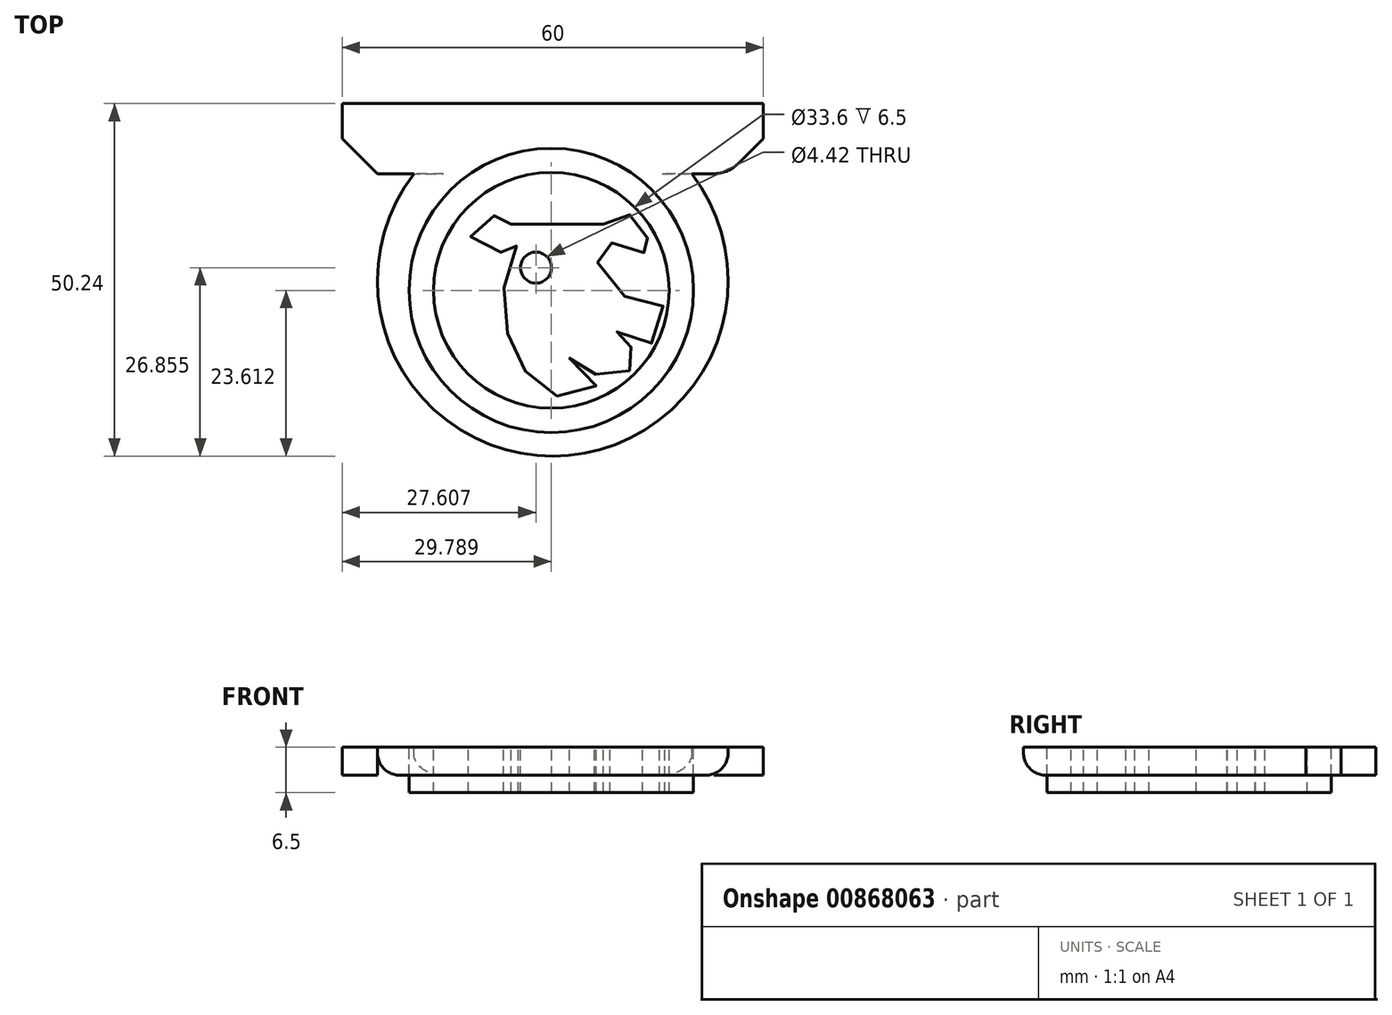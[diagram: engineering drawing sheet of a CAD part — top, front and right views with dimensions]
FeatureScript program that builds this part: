
annotation { "Feature Type Name" : "Feature", "Feature Type Description" : "" }
export const myFeature = defineFeature(function(context is Context, id is Id, definition is map)
    precondition{}
    {
        {
            var Q0;
            Q0=qCreatedBy(makeId("Top.planeOp"),FACE);
            var sketch = newSketch(context, id + "F0", { "sketchPlane" : qUnion([Q0])});
            skCircle(sketch, "E0", {"center": v(0, 1.5) * mm, "radius": 25 * mm});
            skLineSegment(sketch, "E1.bottom", {"start": v(-30, 26.74) * mm, "end": v(30, 26.74) * mm});
            skLineSegment(sketch, "E1.top", {"start": v(-30, 16.74) * mm, "end": v(30, 16.74) * mm});
            skLineSegment(sketch, "E1.left", {"start": v(-30, 26.74) * mm, "end": v(-30, 16.74) * mm});
            skLineSegment(sketch, "E1.right", {"start": v(30, 26.74) * mm, "end": v(30, 16.74) * mm});
            skPoint(sketch, "E1.middle", {"position": v(0, 21.74) * mm});
            skSolve(sketch);
        }
        {
            var Q0;
            Q0=makeQuery(id+"F0.imprint","IMPRINT",FACE,{"disambiguationData":[TD([[makeQuery(id+"F0.imprint","IMPRINT",EDGE,{"derivedFrom":sQuery(id+"F0.wireOp",EDGE,"E0")}),1.0]])]});
            var Q1;
            Q1=makeQuery(id+"F0.imprint","IMPRINT",FACE,{"disambiguationData":[TD([[makeQuery(id+"F0.imprint","IMPRINT",EDGE,{"derivedFrom":sQuery(id+"F0.wireOp",EDGE,"E1.bottom")}),-1.0]])]});
            extrude(context, id + "F1", {"entities" : qUnion([Q0, Q1]), "oppositeDirection" : true, "depth" : 4 * mm, "offsetDistance" : 25 * mm});
        }
        {
            var Q0;
            Q0=makeQuery(id+"F1.opExtrude","CAP_FACE",FACE,{"disambiguationData":[OSD([sQuery(id+"F0.wireOp",EDGE,"E0")])],"isStart":true});
            var sketch = newSketch(context, id + "F2", { "sketchPlane" : qUnion([Q0])});
            skCircle(sketch, "E2", {"center": v(-0.21, 0.11) * mm, "radius": 20.27 * mm});
            skPoint(sketch, "E2.first.point", {"position": v(-20.47, 0.75) * mm});
            skPoint(sketch, "E2.second.point", {"position": v(20.05, 0.75) * mm});
            skPoint(sketch, "E2.third.point", {"position": v(-0.46, 20.38) * mm});
            skCircle(sketch, "E3", {"center": v(-0.21, 0.11) * mm, "radius": 16.8 * mm});
            skCircle(sketch, "E4", {"center": v(-2.4, 3.35) * mm, "radius": 2.21 * mm});
            skPoint(sketch, "E4.first.point", {"position": v(-4.6, 3.44) * mm});
            skPoint(sketch, "E4.second.point", {"position": v(-0.18, 3.4) * mm});
            skPoint(sketch, "E4.third.point", {"position": v(-2.2, 5.56) * mm});
            skLineSegment(sketch, "E5", {"start": v(-5.96, 9.54) * mm, "end": v(7.23, 9.54) * mm});
            skFitSpline(sketch, "E6", {"points": [v(7.23, 9.54) * mm, v(7.52, 9.54) * mm, v(8.13, 9.75) * mm, v(8.6, 10) * mm, v(9.3, 10.53) * mm, v(9.96, 10.81) * mm, v(10.49, 10.9) * mm, v(12.05, 10.88) * mm, v(12.18, 10.8) * mm, v(12.24, 10.54) * mm, v(12.35, 10) * mm, v(12.8, 8.84) * mm, v(13.39, 7.77) * mm, v(14.02, 7.05) * mm, v(14.93, 6.32) * mm, v(15.18, 6.08) * mm, v(15.18, 5.8) * mm, v(15, 5.57) * mm, v(14.59, 5.51) * mm, v(11.17, 5.52) * mm, v(10.84, 5.56) * mm, v(9.87, 6.07) * mm, v(9.26, 6.43) * mm, v(8.83, 6.68) * mm, v(8.46, 6.87) * mm, v(8.15, 6.9) * mm, v(6.14, 6.93) * mm, v(5.99, 6.89) * mm, v(5.94, 6.72) * mm, v(6.03, 5.67) * mm, v(6.36, 4.14) * mm, v(7.07, 2.5) * mm, v(7.98, 1.22) * mm, v(9.03, 0.12) * mm, v(10.34, -0.77) * mm, v(11.98, -1.45) * mm, v(13.56, -1.8) * mm, v(15.11, -1.91) * mm, v(15.54, -2) * mm, v(15.81, -2.25) * mm, v(15.98, -2.58) * mm, v(15.89, -3.16) * mm, v(15.2, -5.45) * mm, v(14.32, -7.16) * mm, v(13.93, -7.48) * mm, v(13.37, -7.6) * mm, v(12.88, -7.57) * mm, v(11.21, -6.97) * mm, v(9.76, -6.18) * mm, v(8.91, -5.67) * mm, v(8.58, -5.62) * mm, v(8.32, -5.74) * mm, v(8.2, -6.01) * mm, v(8.2, -6.3) * mm, v(9.27, -7.05) * mm, v(11.5, -8.1) * mm, v(12.4, -8.43) * mm, v(12.7, -8.7) * mm, v(12.77, -9.26) * mm, v(12.47, -9.87) * mm, v(11.13, -11.17) * mm, v(9.23, -12.6) * mm, v(8.6, -12.92) * mm, v(7.95, -12.97) * mm, v(7.6, -12.91) * mm, v(6.03, -11.78) * mm, v(3.74, -9.66) * mm, v(3.26, -9.1) * mm, v(3.07, -8.95) * mm, v(2.74, -8.94) * mm, v(2.45, -9.2) * mm, v(2.4, -9.52) * mm, v(2.56, -9.8) * mm, v(3.73, -11.02) * mm, v(5.36, -12.51) * mm, v(6.08, -13.09) * mm, v(6.19, -13.4) * mm, v(6.13, -13.76) * mm, v(5.81, -14.15) * mm, v(3.84, -14.68) * mm, v(1.76, -14.9) * mm, v(0.28, -14.9) * mm, v(-0.56, -14.66) * mm, v(-1.5, -14.11) * mm, v(-2.72, -12.9) * mm, v(-3.92, -11.4) * mm, v(-4.9, -9.75) * mm, v(-5.48, -8.54) * mm, v(-5.92, -7.5) * mm, v(-6.35, -6.26) * mm, v(-6.74, -4.64) * mm, v(-6.98, -2.94) * mm, v(-7.03, -0.9) * mm, v(-6.95, 0.57) * mm, v(-6.6, 2.72) * mm, v(-6, 4.61) * mm, v(-5.65, 5.48) * mm, v(-5.2, 6.44) * mm, v(-4.97, 6.84) * mm, v(-4.97, 6.96) * mm, v(-6.14, 6.93) * mm, v(-6.23, 6.9) * mm, v(-6.3, 6.84) * mm, v(-6.58, 6.43) * mm, v(-7.06, 5.74) * mm, v(-7.3, 5.54) * mm, v(-7.97, 5.53) * mm, v(-8.4, 5.63) * mm, v(-9.3, 5.96) * mm, v(-10.3, 6.54) * mm, v(-11.22, 7.28) * mm, v(-12.05, 8.2) * mm, v(-12.03, 8.23) * mm, v(-11.31, 9.03) * mm, v(-10.38, 9.81) * mm, v(-9.23, 10.48) * mm, v(-8.17, 10.82) * mm, v(-7.77, 10.9) * mm, v(-7.1, 10.9) * mm, v(-6.79, 10.69) * mm, v(-6.51, 10.19) * mm, v(-6.4, 9.83) * mm, v(-6.33, 9.64) * mm, v(-6.2, 9.54) * mm, v(-5.96, 9.54) * mm], "startDerivative": vector(55.31, -6.4) * mm, "endDerivative": vector(59.6, 6.66) * mm});
            skSolve(sketch);
        }
        {
            var Q0;
            Q0=makeQuery(id+"F2.imprint","IMPRINT",FACE,{"disambiguationData":[TD([[makeQuery(id+"F2.imprint","IMPRINT",EDGE,{"derivedFrom":sQuery(id+"F2.wireOp",EDGE,"E4")}),-1.0]])]});
            var Q1;
            Q1=makeQuery(id+"F2.imprint","IMPRINT",FACE,{"disambiguationData":[TD([[makeQuery(id+"F2.imprint","IMPRINT",EDGE,{"derivedFrom":sQuery(id+"F2.wireOp",EDGE,"E2")}),1.0]])]});
            var Q2;
            Q2=makeQuery(id+"F1.opExtrude","CAP_FACE",FACE,{"disambiguationData":[OSD([sQuery(id+"F0.wireOp",EDGE,"GiU07cMu-9cvY-aq7m-KHih-6PXQR21th8sj.bottom"),sQuery(id+"F0.wireOp",EDGE,"GiU07cMu-9cvY-aq7m-KHih-6PXQR21th8sj.top"),sQuery(id+"F0.wireOp",EDGE,"GiU07cMu-9cvY-aq7m-KHih-6PXQR21th8sj.left"),sQuery(id+"F0.wireOp",EDGE,"P3Z4kugq-KXoC-PKu6-b1Nk-Jbw3Nn5FDpoZ"),sQuery(id+"F0.wireOp",EDGE,"qLsFG4fF-1ukw-phWH-hEqs-MhgE6pIn2S9s")])],"isStart":true});
            var Q3;
            Q3=makeQuery(id+"F1.opExtrude","SWEPT_BODY",BODY,{"disambiguationData":[OSD([sQuery(id+"F0.wireOp",EDGE,"GiU07cMu-9cvY-aq7m-KHih-6PXQR21th8sj.bottom"),sQuery(id+"F0.wireOp",EDGE,"GiU07cMu-9cvY-aq7m-KHih-6PXQR21th8sj.top"),sQuery(id+"F0.wireOp",EDGE,"GiU07cMu-9cvY-aq7m-KHih-6PXQR21th8sj.left"),sQuery(id+"F0.wireOp",EDGE,"P3Z4kugq-KXoC-PKu6-b1Nk-Jbw3Nn5FDpoZ"),sQuery(id+"F0.wireOp",EDGE,"qLsFG4fF-1ukw-phWH-hEqs-MhgE6pIn2S9s")])]});
            extrude(context, id + "F3", {"entities" : qUnion([Q0, Q1]), "oppositeDirection" : true, "depth" : 6.5 * mm, "endBoundEntityFace" : qUnion([Q2]), "endBoundEntityBody" : qUnion([Q3]), "offsetDistance" : 25 * mm});
        }
        {
            var Q0;
            Q0=makeQuery(id+"F1.opExtrude","SWEPT_EDGE",EDGE,{"disambiguationData":[OSD([sQuery(id+"F0.wireOp",EDGE,"E1.top"),sQuery(id+"F0.wireOp",EDGE,"E1.right")])]});
            var Q1;
            Q1=makeQuery(id+"F1.opExtrude","SWEPT_EDGE",EDGE,{"disambiguationData":[OSD([sQuery(id+"F0.wireOp",EDGE,"E1.top"),sQuery(id+"F0.wireOp",EDGE,"E1.left")])]});
            chamfer(context, id + "F4", {"entities" : qUnion([Q0, Q1]), "width" : 5 * mm, "tangentPropagation" : true});
        }
        {
            var Q0;
            Q0=makeQuery(id+"F1.opExtrude","CAP_EDGE",EDGE,{"disambiguationData":[OSD([sQuery(id+"F0.wireOp",EDGE,"E0")])],"isStart":false});
            fillet(context, id + "F5", {"entities" : qUnion([Q0]), "tangentPropagation" : true, "radius" : 3.2 * mm, "defaultsChanged" : true, "vertexSettings" : [], "allowEdgeOverflow" : false});
        }
        {
            var Q0;
            {var subQ0=sQuery(id+"F0.wireOp",EDGE,"E1.top");var subQ1=sQuery(id+"F0.wireOp",EDGE,"E1.left");Q0=makeQuery(id+"F4.opChamfer","BLEND_EDGE",EDGE,{"blendedFrom":[makeQuery(id+"F1.opExtrude","SWEPT_EDGE",EDGE,{"disambiguationData":[OSD([subQ0,subQ1])]}),makeQuery(id+"F1.opExtrude","SWEPT_FACE",FACE,{"disambiguationData":[OSD([subQ0]),TDD([makeQuery(id+"F0.imprint","IMPRINT",EDGE,{"disambiguationData":[TD([[makeQuery(id+"F0.imprint","INTERSECT",VERTEX,{"disambiguationData":[OD(0.0)],"derivedFrom":[sQuery(id+"F0.wireOp",EDGE,"E0"),subQ0]}),1.0]])],"derivedFrom":subQ0})])]})],"blendedInto":[makeQuery(id+"F1.opExtrude","SWEPT_FACE",FACE,{"disambiguationData":[OSD([subQ0]),TDD([makeQuery(id+"F0.imprint","IMPRINT",EDGE,{"disambiguationData":[TD([[makeQuery(id+"F0.imprint","INTERSECT",VERTEX,{"disambiguationData":[OD(0.0)],"derivedFrom":[sQuery(id+"F0.wireOp",EDGE,"E0"),subQ0]}),1.0]])],"derivedFrom":subQ0})])]})]});}
            var Q1;
            {var subQ0=sQuery(id+"F0.wireOp",EDGE,"E1.right");var subQ1=sQuery(id+"F0.wireOp",EDGE,"E1.top");Q1=makeQuery(id+"F4.opChamfer","BLEND_EDGE",EDGE,{"blendedFrom":[makeQuery(id+"F1.opExtrude","SWEPT_EDGE",EDGE,{"disambiguationData":[OSD([subQ1,subQ0])]}),makeQuery(id+"F1.opExtrude","SWEPT_FACE",FACE,{"disambiguationData":[OSD([subQ1]),TDD([makeQuery(id+"F0.imprint","IMPRINT",EDGE,{"disambiguationData":[TD([[makeQuery(id+"F0.imprint","INTERSECT",VERTEX,{"derivedFrom":[subQ1,subQ0]}),1.0]])],"derivedFrom":subQ1})])]})],"blendedInto":[makeQuery(id+"F1.opExtrude","SWEPT_FACE",FACE,{"disambiguationData":[OSD([subQ1]),TDD([makeQuery(id+"F0.imprint","IMPRINT",EDGE,{"disambiguationData":[TD([[makeQuery(id+"F0.imprint","INTERSECT",VERTEX,{"derivedFrom":[subQ1,subQ0]}),1.0]])],"derivedFrom":subQ1})])]})]});}
            fillet(context, id + "F6", {"entities" : qUnion([Q0, Q1]), "tangentPropagation" : true, "radius" : 5 * mm, "defaultsChanged" : false, "vertexSettings" : [], "allowEdgeOverflow" : false});
        }
    });
